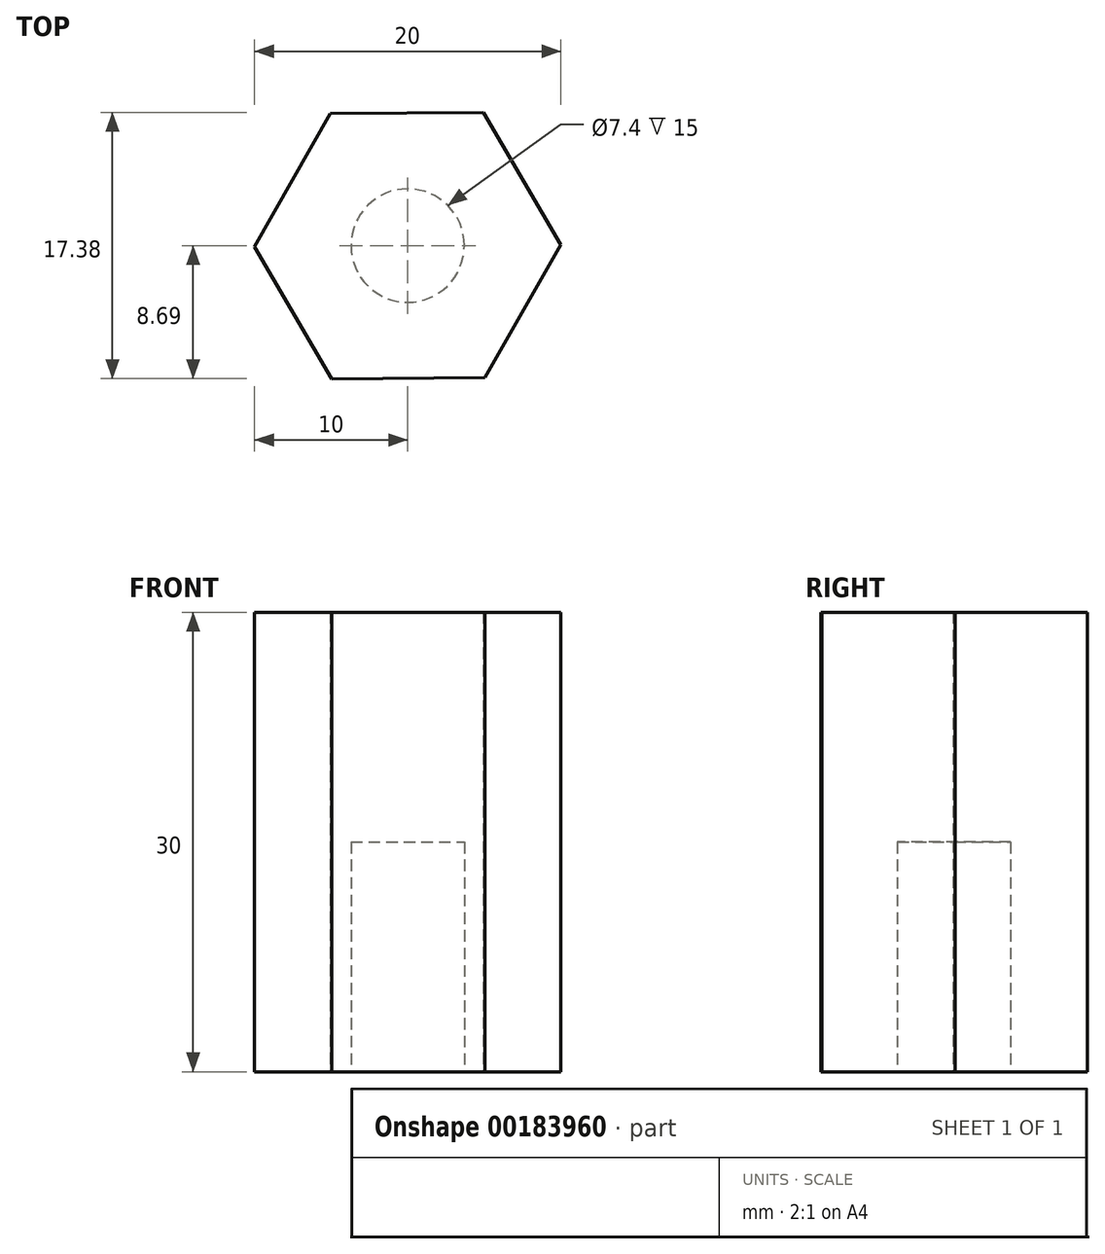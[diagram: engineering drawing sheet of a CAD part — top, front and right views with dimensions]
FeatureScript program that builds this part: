
annotation { "Feature Type Name" : "Feature", "Feature Type Description" : "" }
export const myFeature = defineFeature(function(context is Context, id is Id, definition is map)
    precondition{}
    {
        {
            var Q0;
            Q0=qCreatedBy(makeId("Top.planeOp"),FACE);
            var sketch = newSketch(context, id + "F0", { "sketchPlane" : qUnion([Q0])});
            skCircle(sketch, "E0.cCircle", {"center": v(0, 0) * mm, "radius": 10 * mm, "construction": true});
            skLineSegment(sketch, "E0.0", {"start": v(-5.06, 8.63) * mm, "end": v(4.94, 8.7) * mm});
            skLineSegment(sketch, "E0.1", {"start": v(4.94, 8.7) * mm, "end": v(10, 0.06) * mm});
            skLineSegment(sketch, "E0.2", {"start": v(10, 0.06) * mm, "end": v(5.06, -8.63) * mm});
            skLineSegment(sketch, "E0.3", {"start": v(5.06, -8.63) * mm, "end": v(-4.94, -8.7) * mm});
            skLineSegment(sketch, "E0.4", {"start": v(-4.94, -8.7) * mm, "end": v(-10, -0.06) * mm});
            skLineSegment(sketch, "E0.5", {"start": v(-10, -0.06) * mm, "end": v(-5.06, 8.63) * mm});
            skSolve(sketch);
        }
        {
            var Q0;
            Q0 = qSketchRegion(id + "F0", true);
            extrude(context, id + "F1", {"entities" : qUnion([Q0]), "depth" : 30 * mm});
        }
        {
            var Q0;
            Q0=makeQuery(id+"F1.opExtrude","CAP_FACE",FACE,{"disambiguationData":[OSD([sQuery(id+"F0.wireOp",EDGE,"E0.0"),sQuery(id+"F0.wireOp",EDGE,"E0.1"),sQuery(id+"F0.wireOp",EDGE,"E0.2"),sQuery(id+"F0.wireOp",EDGE,"E0.3"),sQuery(id+"F0.wireOp",EDGE,"E0.4"),sQuery(id+"F0.wireOp",EDGE,"E0.5")])],"isStart":true});
            var sketch = newSketch(context, id + "F2", { "sketchPlane" : qUnion([Q0])});
            skCircle(sketch, "E1", {"center": v(0, 0) * mm, "radius": 3.7 * mm});
            skSolve(sketch);
        }
        {
            var Q0;
            Q0 = qSketchRegion(id + "F2", true);
            extrude(context, id + "F3", {"entities" : qUnion([Q0]), "operationType" : NewBodyOperationType.REMOVE, "oppositeDirection" : true, "depth" : 15 * mm});
        }
    });
